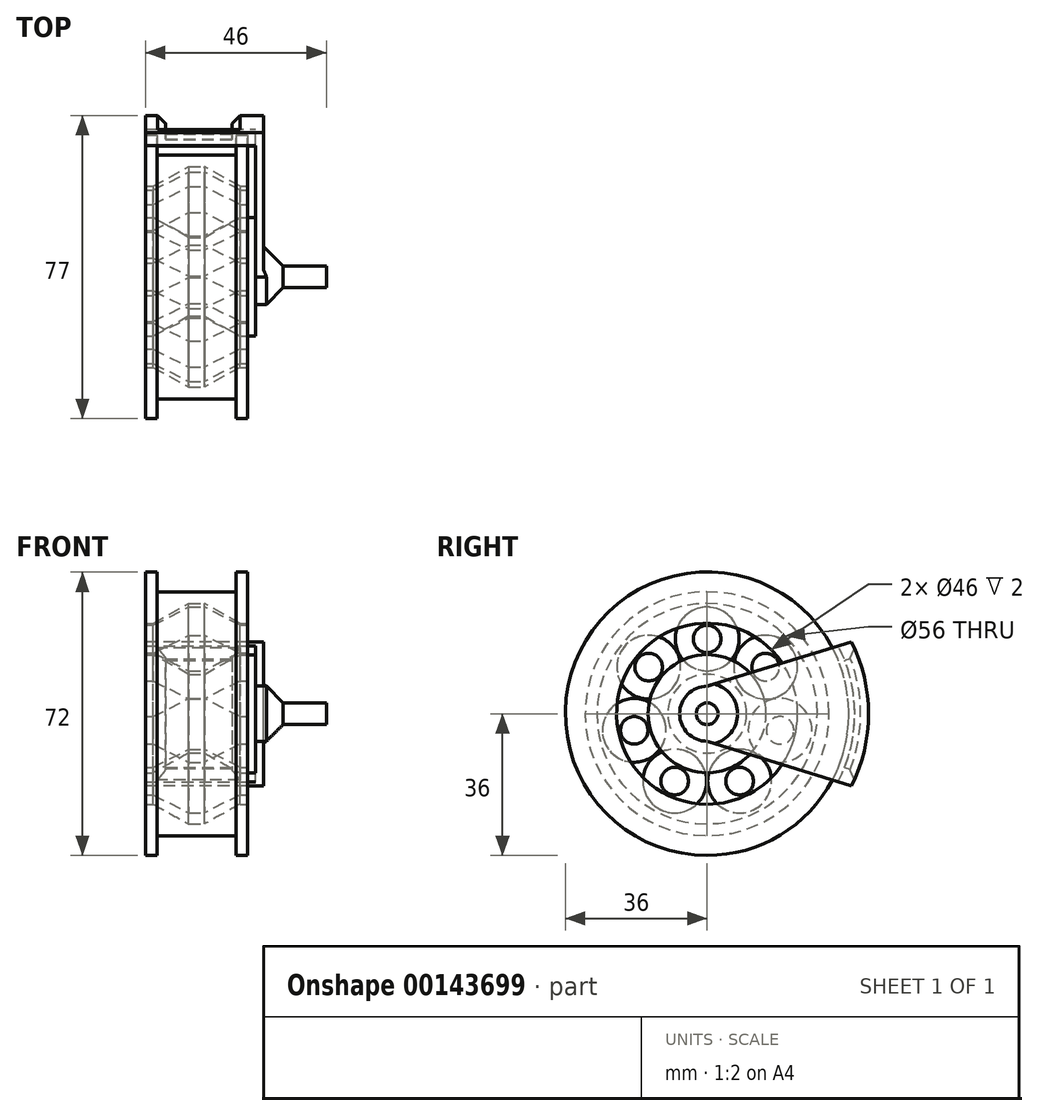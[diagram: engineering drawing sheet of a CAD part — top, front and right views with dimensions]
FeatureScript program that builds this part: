
annotation { "Feature Type Name" : "Feature", "Feature Type Description" : "" }
export const myFeature = defineFeature(function(context is Context, id is Id, definition is map)
    precondition{}
    {
        {
            var Q0;
            Q0=qCreatedBy(makeId("Right.planeOp"),FACE);
            var sketch = newSketch(context, id + "F0", { "sketchPlane" : qUnion([Q0])});
            skCircle(sketch, "E0", {"center": v(0, 0) * mm, "radius": 30 * mm});
            skCircle(sketch, "E1", {"center": v(0, 0) * mm, "radius": 28 * mm});
            skSolve(sketch);
        }
        {
            var Q0;
            Q0=qCreatedBy(makeId("Front.planeOp"),FACE);
            var sketch = newSketch(context, id + "F1", { "sketchPlane" : qUnion([Q0])});
            skLineSegment(sketch, "E2", {"start": v(0, 31) * mm, "end": v(10, 31) * mm});
            skLineSegment(sketch, "E3", {"start": v(13, 31) * mm, "end": v(13, 23) * mm});
            skLineSegment(sketch, "E4", {"start": v(13, 23) * mm, "end": v(11, 23) * mm});
            skLineSegment(sketch, "E5", {"start": v(11, 23) * mm, "end": v(2, 28) * mm});
            skLineSegment(sketch, "E6", {"start": v(2, 28) * mm, "end": v(0, 28) * mm});
            skLineSegment(sketch, "E7", {"start": v(13, 31) * mm, "end": v(13, 36) * mm});
            skLineSegment(sketch, "E8", {"start": v(13, 36) * mm, "end": v(10, 36) * mm});
            skLineSegment(sketch, "E9", {"start": v(10, 36) * mm, "end": v(10, 31) * mm});
            skLineSegment(sketch, "E10.MirrorCS", {"start": v(-10, 36) * mm, "end": v(-10, 31) * mm});
            skLineSegment(sketch, "E11.MirrorCS", {"start": v(-13, 31) * mm, "end": v(-13, 36) * mm});
            skLineSegment(sketch, "E12.MirrorCS", {"start": v(-2, 28) * mm, "end": v(0, 28) * mm});
            skLineSegment(sketch, "E13.MirrorCS", {"start": v(0, 31) * mm, "end": v(-10, 31) * mm});
            skLineSegment(sketch, "E14.MirrorCS", {"start": v(-11, 23) * mm, "end": v(-2, 28) * mm});
            skLineSegment(sketch, "E15.MirrorCS", {"start": v(-13, 31) * mm, "end": v(-13, 23) * mm});
            skLineSegment(sketch, "E16.MirrorCS", {"start": v(-13, 23) * mm, "end": v(-11, 23) * mm});
            skLineSegment(sketch, "E17.MirrorCS", {"start": v(-13, 36) * mm, "end": v(-10, 36) * mm});
            skLineSegment(sketch, "E18", {"start": v(24.96, 0) * mm, "end": v(-29.42, 0) * mm, "construction": true});
            skSolve(sketch);
        }
        {
            var Q0;
            Q0=makeQuery(id+"F1.imprint","IMPRINT",FACE,{"disambiguationData":[TD([[makeQuery(id+"F1.imprint","IMPRINT",EDGE,{"derivedFrom":sQuery(id+"F1.wireOp",EDGE,"E2")}),-1.0]])]});
            var Q1;
            Q1=sQuery(id+"F1.wireOp",EDGE,"E7");
            var Q2;
            Q2=sQuery(id+"F1.wireOp",EDGE,"E10.MirrorCS");
            var Q3;
            Q3=sQuery(id+"F1.wireOp",EDGE,"E11.MirrorCS");
            var Q4;
            Q4=sQuery(id+"F1.wireOp",EDGE,"E14.MirrorCS");
            var Q5;
            Q5=sQuery(id+"F1.wireOp",EDGE,"E6");
            var Q6;
            Q6=sQuery(id+"F1.wireOp",EDGE,"E9");
            var Q7;
            Q7=sQuery(id+"F1.wireOp",EDGE,"E12.MirrorCS");
            var Q8;
            Q8=sQuery(id+"F1.wireOp",EDGE,"E5");
            var Q9;
            Q9=sQuery(id+"F1.wireOp",EDGE,"E13.MirrorCS");
            var Q10;
            Q10=sQuery(id+"F1.wireOp",EDGE,"E3");
            var Q11;
            Q11=sQuery(id+"F1.wireOp",EDGE,"E2");
            var Q12;
            Q12=sQuery(id+"F1.wireOp",EDGE,"E17.MirrorCS");
            var Q13;
            Q13=sQuery(id+"F1.wireOp",EDGE,"E15.MirrorCS");
            var Q14;
            Q14=sQuery(id+"F1.wireOp",EDGE,"E8");
            var Q15;
            Q15=sQuery(id+"F1.wireOp",EDGE,"E4");
            var Q16;
            Q16=sQuery(id+"F1.wireOp",EDGE,"E16.MirrorCS");
            var Q17;
            Q17=sQuery(id+"F1.wireOp",EDGE,"E18");
            revolve(context, id + "F2", {"entities" : qUnion([Q0]), "surfaceEntities" : qUnion([Q1, Q2, Q3, Q4, Q5, Q6, Q7, Q8, Q9, Q10, Q11, Q12, Q13, Q14, Q15, Q16]), "axis" : qUnion([Q17]), "revolveType" : RevolveType.FULL});
        }
        {
            var Q0;
            Q0=qCreatedBy(makeId("Front.planeOp"),FACE);
            var sketch = newSketch(context, id + "F3", { "sketchPlane" : qUnion([Q0])});
            skLineSegment(sketch, "E19", {"start": v(0, 10) * mm, "end": v(2, 10) * mm});
            skLineSegment(sketch, "E20", {"start": v(2, 10) * mm, "end": v(11, 15) * mm});
            skLineSegment(sketch, "E21", {"start": v(11, 15) * mm, "end": v(13, 15) * mm});
            skLineSegment(sketch, "E22", {"start": v(13, 0) * mm, "end": v(0, 0) * mm});
            skLineSegment(sketch, "E23.MirrorCS", {"start": v(-11, 15) * mm, "end": v(-13, 15) * mm});
            skLineSegment(sketch, "E24.MirrorCS", {"start": v(-2, 10) * mm, "end": v(-11, 15) * mm});
            skLineSegment(sketch, "E25.MirrorCS", {"start": v(-13, 15) * mm, "end": v(-13, 0) * mm});
            skLineSegment(sketch, "E26.MirrorCS", {"start": v(-13, 0) * mm, "end": v(0, 0) * mm});
            skLineSegment(sketch, "E27.MirrorCS", {"start": v(0, 10) * mm, "end": v(-2, 10) * mm});
            skLineSegment(sketch, "E28.bottom", {"start": v(13, 0) * mm, "end": v(15, 0) * mm});
            skLineSegment(sketch, "E28.top", {"start": v(13, 15) * mm, "end": v(15, 15) * mm});
            skLineSegment(sketch, "E28.right", {"start": v(15, 0) * mm, "end": v(15, 15) * mm});
            skSolve(sketch);
        }
        {
            var Q0;
            Q0 = qSketchRegion(id + "F3", true);
            var Q1;
            Q1=sQuery(id+"F1.wireOp",EDGE,"E18");
            revolve(context, id + "F4", {"entities" : qUnion([Q0]), "axis" : qUnion([Q1]), "revolveType" : RevolveType.FULL});
        }
        {
            var Q0;
            Q0=qCreatedBy(makeId("Front.planeOp"),FACE);
            var sketch = newSketch(context, id + "F5", { "sketchPlane" : qUnion([Q0])});
            skLineSegment(sketch, "E29", {"start": v(0, 27.1) * mm, "end": v(2, 27.1) * mm});
            skLineSegment(sketch, "E30", {"start": v(2, 27.1) * mm, "end": v(11, 22.5) * mm});
            skLineSegment(sketch, "E31", {"start": v(11, 22.5) * mm, "end": v(13, 22.5) * mm});
            skLineSegment(sketch, "E32", {"start": v(13, 22.5) * mm, "end": v(13, 19) * mm});
            skLineSegment(sketch, "E33.MirrorCS", {"start": v(-13, 22.5) * mm, "end": v(-13, 19) * mm});
            skLineSegment(sketch, "E34.MirrorCS", {"start": v(-11, 22.5) * mm, "end": v(-13, 22.5) * mm});
            skLineSegment(sketch, "E35.MirrorCS", {"start": v(0, 27.1) * mm, "end": v(-2, 27.1) * mm});
            skLineSegment(sketch, "E36.MirrorCS", {"start": v(-2, 27.1) * mm, "end": v(-11, 22.5) * mm});
            skLineSegment(sketch, "E37", {"start": v(-13, 19) * mm, "end": v(13, 19) * mm});
            skSolve(sketch);
        }
        {
            var Q0;
            Q0=makeQuery(id+"F5.imprint","IMPRINT",FACE,{"disambiguationData":[TD([[makeQuery(id+"F5.imprint","IMPRINT",EDGE,{"derivedFrom":sQuery(id+"F5.wireOp",EDGE,"E29")}),-1.0]])]});
            var Q1;
            Q1=sQuery(id+"F5.wireOp",EDGE,"E29");
            var Q2;
            Q2=sQuery(id+"F5.wireOp",EDGE,"E30");
            var Q3;
            Q3=sQuery(id+"F5.wireOp",EDGE,"E31");
            var Q4;
            Q4=sQuery(id+"F5.wireOp",EDGE,"E32");
            var Q5;
            Q5=sQuery(id+"F5.wireOp",EDGE,"E30");
            var Q6;
            Q6=sQuery(id+"F5.wireOp",EDGE,"E35.MirrorCS");
            var Q7;
            Q7=sQuery(id+"F5.wireOp",EDGE,"E36.MirrorCS");
            var Q8;
            Q8=sQuery(id+"F5.wireOp",EDGE,"E34.MirrorCS");
            var Q9;
            Q9=sQuery(id+"F5.wireOp",EDGE,"E33.MirrorCS");
            var Q10;
            Q10=sQuery(id+"F5.wireOp",EDGE,"E37");
            revolve(context, id + "F6", {"entities" : qUnion([Q0]), "surfaceEntities" : qUnion([Q1, Q2, Q3, Q4, Q5, Q6, Q7, Q8, Q9]), "axis" : qUnion([Q10]), "revolveType" : RevolveType.FULL, "oppositeDirection" : true});
        }
        {
            var Q0;
            Q0=makeQuery(id+"F6.opRevolve","SWEPT_BODY",BODY,{"disambiguationData":[OSD([sQuery(id+"F5.wireOp",EDGE,"E33.MirrorCS")])]});
            var Q1;
            Q1=sQuery(id+"F3.wireOp",EDGE,"E22");
            circularPattern(context, id + "F7", {"entities" : qUnion([Q0]), "axis" : qUnion([Q1]), "angle" : 360 * degree, "instanceCount" : 7, "equalSpace" : true});
        }
        {
            var Q0;
            Q0=makeQuery(id+"F4.opRevolve","SWEPT_FACE",FACE,{"disambiguationData":[OSD([sQuery(id+"F3.wireOp",EDGE,"E28.right")])]});
            var sketch = newSketch(context, id + "F8", { "sketchPlane" : qUnion([Q0])});
            skCircle(sketch, "E38", {"center": v(0, 0) * mm, "radius": 2.75 * mm});
            skSolve(sketch);
        }
        {
            var Q0;
            Q0 = qSketchRegion(id + "F8", true);
            extrude(context, id + "F9", {"entities" : qUnion([Q0]), "depth" : 18 * mm});
        }
        {
            var Q0;
            Q0=makeQuery(id+"F4.opRevolve","SWEPT_FACE",FACE,{"disambiguationData":[OSD([sQuery(id+"F3.wireOp",EDGE,"E28.right")])]});
            var sketch = newSketch(context, id + "F10", { "sketchPlane" : qUnion([Q0])});
            skArc(sketch, "E39", {"start": v(0, 7) * mm, "mid": v(-7, 0) * mm, "end": v(0, -7) * mm});
            skArc(sketch, "E40", {"start": v(42, -20) * mm, "mid": v(62, -0.19) * mm, "end": v(42.37, 20) * mm});
            skLineSegment(sketch, "E41", {"start": v(0, 7) * mm, "end": v(36.7, 18.26) * mm});
            skLineSegment(sketch, "E42", {"start": v(0, -7) * mm, "end": v(36.67, -18.35) * mm});
            skArc(sketch, "E43", {"start": v(36.67, -18.35) * mm, "mid": v(41, -0.05) * mm, "end": v(36.7, 18.26) * mm});
            skSolve(sketch);
        }
        {
            var Q0;
            {var subQ1=sQuery(id+"F10.wireOp",EDGE,"E39");Q0=makeQuery(id+"F10.imprint","IMPRINT",FACE,{"disambiguationData":[TD([[makeQuery(id+"F10.imprint","IMPRINT",EDGE,{"derivedFrom":subQ1}),1.0]])]});}
            var Q1;
            {var subQ0=sQuery(id+"F10.wireOp",EDGE,"E43");Q1=makeQuery(id+"F10.imprint","IMPRINT",FACE,{"disambiguationData":[TD([[makeQuery(id+"F10.imprint","IMPRINT",EDGE,{"derivedFrom":subQ0}),1.0]])]});}
            extrude(context, id + "F11", {"entities" : qUnion([Q0, Q1]), "operationType" : NewBodyOperationType.ADD, "depth" : 2 * mm});
        }
        {
            var Q0;
            Q0=makeQuery(id+"F11.opExtrude","CAP_FACE",FACE,{"disambiguationData":[OSD([sQuery(id+"F8.wireOp",EDGE,"E38"),sQuery(id+"F10.wireOp",EDGE,"E39"),sQuery(id+"F10.wireOp",EDGE,"E41"),sQuery(id+"F10.wireOp",EDGE,"E42"),sQuery(id+"F10.wireOp",EDGE,"E43")])],"isStart":false});
            var sketch = newSketch(context, id + "F12", { "sketchPlane" : qUnion([Q0])});
            skCircle(sketch, "E44", {"center": v(0, 0) * mm, "radius": 41 * mm});
            skCircle(sketch, "E45", {"center": v(0, 0) * mm, "radius": 37.5 * mm});
            skLineSegment(sketch, "E46", {"start": v(36.7, 18.26) * mm, "end": v(33.31, 17.22) * mm});
            skLineSegment(sketch, "E47", {"start": v(34.96, 13.57) * mm, "end": v(38.31, 14.6) * mm});
            skLineSegment(sketch, "E48", {"start": v(33.27, -17.3) * mm, "end": v(36.67, -18.35) * mm});
            skLineSegment(sketch, "E49", {"start": v(34.93, -13.66) * mm, "end": v(38.28, -14.69) * mm});
            skSolve(sketch);
        }
        {
            var Q0;
            {var subQ0=sQuery(id+"F12.wireOp",EDGE,"E46");Q0=makeQuery(id+"F12.imprint","IMPRINT",FACE,{"disambiguationData":[TD([[makeQuery(id+"F12.imprint","IMPRINT",EDGE,{"derivedFrom":subQ0}),-1.0]])]});}
            var Q1;
            {var subQ0=sQuery(id+"F12.wireOp",EDGE,"E48");Q1=makeQuery(id+"F12.imprint","IMPRINT",FACE,{"disambiguationData":[TD([[makeQuery(id+"F12.imprint","IMPRINT",EDGE,{"derivedFrom":subQ0}),1.0]])]});}
            extrude(context, id + "F13", {"entities" : qUnion([Q0, Q1]), "operationType" : NewBodyOperationType.ADD, "oppositeDirection" : true, "depth" : 30 * mm});
        }
        {
            var Q0;
            Q0=makeQuery(id+"F13.opExtrude","SWEPT_FACE",FACE,{"disambiguationData":[OSD([sQuery(id+"F12.wireOp",EDGE,"E47")])]});
            var sketch = newSketch(context, id + "F14", { "sketchPlane" : qUnion([Q0])});
            skLineSegment(sketch, "E50.bottom", {"start": v(-13, -40.9) * mm, "end": v(-7.83, -40.9) * mm});
            skLineSegment(sketch, "E50.top", {"start": v(-13, -37.4) * mm, "end": v(-7.83, -37.4) * mm});
            skLineSegment(sketch, "E50.left", {"start": v(-13, -40.9) * mm, "end": v(-13, -37.4) * mm});
            skLineSegment(sketch, "E50.right", {"start": v(-7.83, -40.9) * mm, "end": v(-7.83, -37.4) * mm});
            skSolve(sketch);
        }
        {
            var Q0;
            Q0=makeQuery(id+"F4.opRevolve","SWEPT_FACE",FACE,{"disambiguationData":[OSD([sQuery(id+"F3.wireOp",EDGE,"E25.MirrorCS")])]});
            var sketch = newSketch(context, id + "F15", { "sketchPlane" : qUnion([Q0])});
            skArc(sketch, "E51", {"start": v(-38.3, 14.65) * mm, "mid": v(-40.97, -1.5) * mm, "end": v(-37.12, -17.4) * mm});
            skLineSegment(sketch, "E52", {"start": v(0, 0) * mm, "end": v(-38.3, 14.65) * mm});
            skLineSegment(sketch, "E53", {"start": v(0, 0) * mm, "end": v(-37.12, -17.4) * mm});
            skSolve(sketch);
        }
        {
            var Q0;
            Q0=makeQuery(id+"F14.imprint","IMPRINT",FACE,{"disambiguationData":[TD([[makeQuery(id+"F14.imprint","IMPRINT",EDGE,{"derivedFrom":sQuery(id+"F14.wireOp",EDGE,"E50.bottom")}),1.0]])]});
            var Q1;
            Q1=sQuery(id+"F15.wireOp",EDGE,"E51");
            sweep(context, id + "F16", {"operationType" : NewBodyOperationType.ADD, "profiles" : qUnion([Q0]), "path" : qUnion([Q1])});
        }
        {
            var Q0;
            Q0=makeQuery(id+"F11.opExtrude","CAP_FACE",FACE,{"disambiguationData":[OSD([sQuery(id+"F8.wireOp",EDGE,"E38"),sQuery(id+"F10.wireOp",EDGE,"E39"),sQuery(id+"F10.wireOp",EDGE,"E41"),sQuery(id+"F10.wireOp",EDGE,"E42"),sQuery(id+"F10.wireOp",EDGE,"E43")])],"isStart":true});
            var sketch = newSketch(context, id + "F17", { "sketchPlane" : qUnion([Q0])});
            skCircle(sketch, "E54", {"center": v(0, 0) * mm, "radius": 37.5 * mm});
            skCircle(sketch, "E55", {"center": v(0, 0) * mm, "radius": 41 * mm});
            skLineSegment(sketch, "E56", {"start": v(-34.96, 13.57) * mm, "end": v(-38.31, 14.6) * mm});
            skLineSegment(sketch, "E57", {"start": v(-34.93, -13.66) * mm, "end": v(-38.28, -14.69) * mm});
            skSolve(sketch);
        }
        {
            var Q0;
            Q0=makeQuery(id+"F17.imprint","IMPRINT",FACE,{"disambiguationData":[TD([[makeQuery(id+"F17.imprint","IMPRINT",EDGE,{"disambiguationData":[OD(0.0)],"derivedFrom":sQuery(id+"F17.wireOp",EDGE,"E55")}),-1.0]])]});
            extrude(context, id + "F18", {"entities" : qUnion([Q0]), "operationType" : NewBodyOperationType.ADD, "depth" : 6 * mm});
        }
        {
            var Q0;
            Q0=makeQuery(id+"F11.boolean.opBoolean","INTERSECT",EDGE,{"derivedFrom":[makeQuery(id+"F9.opExtrude","SWEPT_FACE",FACE,{"disambiguationData":[OSD([sQuery(id+"F8.wireOp",EDGE,"E38")])]}),makeQuery(id+"F11.opExtrude","CAP_FACE",FACE,{"disambiguationData":[OSD([sQuery(id+"F10.wireOp",EDGE,"E39"),sQuery(id+"F10.wireOp",EDGE,"E41"),sQuery(id+"F10.wireOp",EDGE,"E42"),sQuery(id+"F10.wireOp",EDGE,"E43")])],"isStart":false})]});
            chamfer(context, id + "F19", {"entities" : qUnion([Q0]), "width" : 5 * mm, "tangentPropagation" : true});
        }
        {
            var Q0;
            Q0=makeQuery(id+"F13.opExtrude","SWEPT_EDGE",EDGE,{"disambiguationData":[OSD([sQuery(id+"F12.wireOp",EDGE,"E44"),sQuery(id+"F12.wireOp",EDGE,"E49")])]});
            var Q1;
            Q1=makeQuery(id+"F18.opExtrude","CAP_EDGE",EDGE,{"disambiguationData":[OSD([sQuery(id+"F17.wireOp",EDGE,"E55")])],"isStart":false});
            var Q2;
            Q2=makeQuery(id+"F13.opExtrude","SWEPT_EDGE",EDGE,{"disambiguationData":[OSD([sQuery(id+"F12.wireOp",EDGE,"E44"),sQuery(id+"F12.wireOp",EDGE,"E47")])]});
            var Q3;
            Q3=makeQuery(id+"F16.opSweep","SWEPT_EDGE",EDGE,{"disambiguationData":[OSD([sQuery(id+"F12.wireOp",EDGE,"E44"),sQuery(id+"F12.wireOp",EDGE,"E47"),sQuery(id+"F14.wireOp",EDGE,"E50.bottom"),sQuery(id+"F14.wireOp",EDGE,"E50.right"),sQuery(id+"F15.wireOp",EDGE,"E51")])]});
            chamfer(context, id + "F20", {"entities" : qUnion([Q0, Q1, Q2, Q3]), "width" : 2 * mm});
        }
    });
